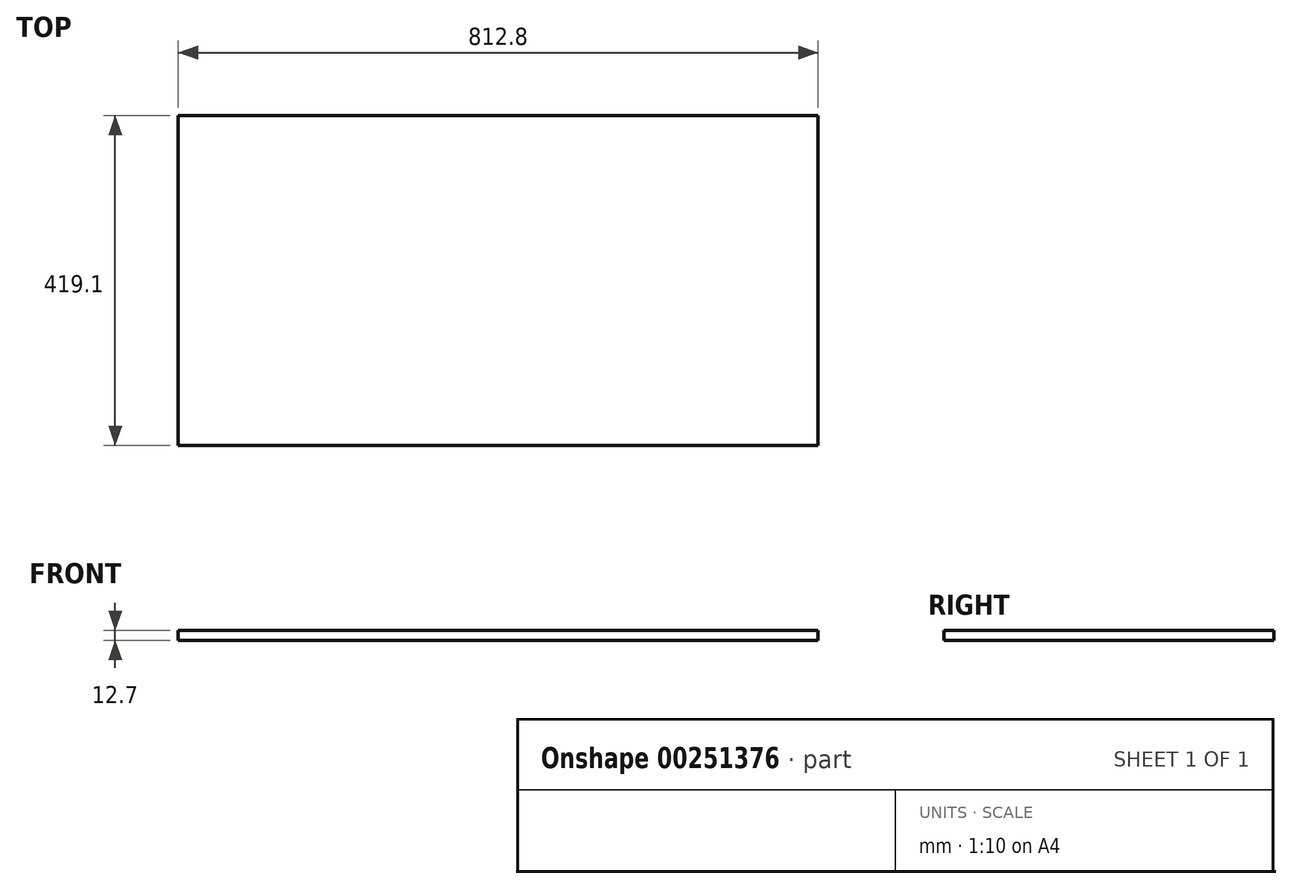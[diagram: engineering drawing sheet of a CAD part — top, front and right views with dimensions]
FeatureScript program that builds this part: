
annotation { "Feature Type Name" : "Feature", "Feature Type Description" : "" }
export const myFeature = defineFeature(function(context is Context, id is Id, definition is map)
    precondition{}
    {
        {
            var Q0;
            Q0=qCreatedBy(makeId("Top.planeOp"),FACE);
            var sketch = newSketch(context, id + "F0", { "sketchPlane" : qUnion([Q0])});
            skLineSegment(sketch, "E0.bottom", {"start": v(-406.4, 209.55) * mm, "end": v(406.4, 209.55) * mm});
            skLineSegment(sketch, "E0.top", {"start": v(-406.4, -209.55) * mm, "end": v(406.4, -209.55) * mm});
            skLineSegment(sketch, "E0.left", {"start": v(-406.4, 209.55) * mm, "end": v(-406.4, -209.55) * mm});
            skLineSegment(sketch, "E0.right", {"start": v(406.4, 209.55) * mm, "end": v(406.4, -209.55) * mm});
            skPoint(sketch, "E0.middle", {"position": v(0, 0) * mm});
            skSolve(sketch);
        }
        {
            var Q0;
            Q0 = qSketchRegion(id + "F0", true);
            extrude(context, id + "F1", {"entities" : qUnion([Q0]), "depth" : 12.7 * mm});
        }
    });
